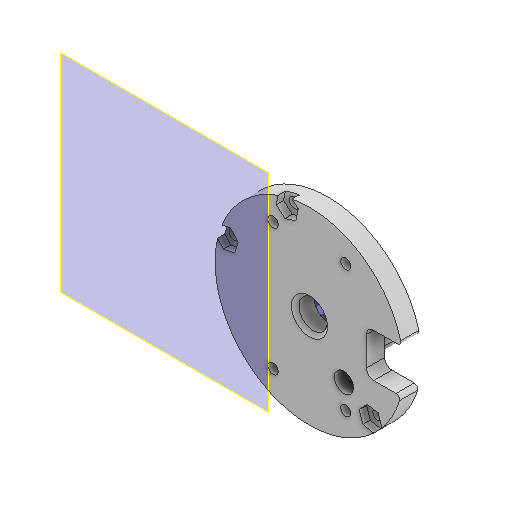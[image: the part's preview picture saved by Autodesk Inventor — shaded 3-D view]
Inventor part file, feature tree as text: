
AUTODESK INVENTOR PART (.ipt)
format: ipt  version: 2022 (Build 260153000, 153)  size: 528,384 bytes
history: native  units: in
note: dims shown in document units (in); Inventor stores cm internally (conversion verified against a paired STEP export)
features: reference x11, extrude x9, sketch x8, other x6, plane x4, projected_geometry x2, fillet x1, chamfer x1
ambient origin geometry x8: Origin, YZ Plane, XZ Plane, XY Plane, X Axis, Y Axis, Z Axis, Center Point
bodies: Solid1 (feature_tree)
feature tree (42):
  plane  "Work Plane1"
  extrude  "Extrusion1"  Depth=0.315in
  extrude  "Extrusion2"  Depth=1.0in
  plane  "Arbeitsebene4"
  extrude  "Extrusion5"  TaperAngle=0.0deg  [1 undecoded]
  plane  "Arbeitsebene3"
  extrude  "Extrusion6"  Depth=0.1102in
  plane  "Arbeitsebene2"
  extrude  "Extrusion7"  Depth=0.0787in
  extrude  "Extrusion10"  Depth=0.0394in TaperAngle=0.0deg
  extrude  "Extrusion11"  Depth=0.3937in
  extrude  "Extrusion12"  Depth=0.0787in
  fillet  "Rundung1"  Radius=0.2165in
  extrude  "Extrusion13"  Depth=0.0787in
  chamfer  "Fase4"  Distance=0.0787in
  sketch  "Sketch1"  dims[d0=0.1969in d1=0.0in d2=0.315in]
  reference  "Reference1"
  reference  "Reference2"
  reference  "Reference3"
  reference  "Reference4"
  reference  "Reference5"
  reference  "Reference6"
  reference  "Reference7"
  reference  "Reference8"
  sketch  "Sketch2"  dims[d3=0.311in d4=1.0in d5=-0.0137in]
  sketch  "Sketch7"  dims[d30=0.1102in d31=0.0in d32=0.0in]
  sketch  "Sketch8"  dims[d33=0.1102in d34=0.1102in]
  sketch  "Sketch9"  dims[d35=0.0in d36=0.0in d37=0.0787in]
  sketch  "Skizze12"  dims[d38=0.0004in d39=0.0in d51=0.0394in d52=0.0in]
  sketch  "Skizze14"  dims[d53=0.2638in d54=0.3937in]
  reference  "Referenz27"
  reference  "Referenz28"
  reference  "Referenz29"
  projected_geometry  "Projizierte Kontur2"
  sketch  "Skizze15"  dims[d55=0.3543in d56=0.0in d60=0.2165in d61=0.2165in d62=0.2165in d63=0.0787in d64=0.0in d65=0.7165in d66=0.7165in d67=0.0787in d68=0.0787in d69=0.3543in d70=0.0in d71=0.315in d72=0.315in d73=0.315in d74=0.315in d75=0.0394in d76=0.0787in d77=45.0deg]
  projected_geometry  "Projizierte Kontur3"
  other  "Assembly1"
  other  "Assembly_MANATEE_V0_Manatee_middle2_v0_18:1"
  other  "Matchboxscope_VCM_v1.iam"
  other  "DIN 912 - ersetzt durch DIN EN ISO 4762 M3 x 25:2"
  other  "DIN 912 - ersetzt durch DIN EN ISO 4762 M3 x 25:1"
  other  "DIN 912 - ersetzt durch DIN EN ISO 4762 M3 x 25:3"
note: 1 required parameter value undecoded (feature->parameter linkage not recoverable at this tier; creation-order binding heuristic only, values carry confidence <= 0.55)
